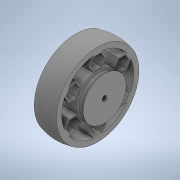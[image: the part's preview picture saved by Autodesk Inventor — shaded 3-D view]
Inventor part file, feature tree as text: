
AUTODESK INVENTOR PART (.ipt)
format: ipt  version: 2020 (Build 240168000, 168)  size: 355,328 bytes
history: native  units: in
note: dims shown in document units (in); Inventor stores cm internally (conversion verified against a paired STEP export)
features: sketch x4, extrude x2, revolve x2, projected_geometry x1
ambient origin geometry x8: Origin, YZ Plane, XZ Plane, XY Plane, X Axis, Y Axis, Z Axis, Center Point
bodies: Solid1 (feature_tree)
feature tree (9):
  extrude  "Extrusion1"  Depth=0.0394in
  sketch  "Sketch3"  dims[d6=0.9843in d7=0.1575in]
  revolve  "Revolution1"  [1 undecoded]
  extrude  "Extrusion2"  Depth=0.1575in
  revolve  "Revolution2"  [1 undecoded]
  sketch  "Sketch1"  dims[d0=0.1181in d1=0.0394in]
  sketch  "Sketch2"  dims[d3=1.8898in d4=0.1181in]
  projected_geometry  "Projected Loop1"
  sketch  "Sketch4"  dims[d8=0.0in d9=1.8898in d10=0.1181in d11=0.0315in d12=2.3622in d14=360.0deg d16=0.5118in d17=0.0in d19=360.0deg d20=0.0787in d24=0.0394in d25=90.0deg d26=45.0deg d28=0.0079in]
note: 2 required parameter values undecoded (feature->parameter linkage not recoverable at this tier; creation-order binding heuristic only, values carry confidence <= 0.55)
